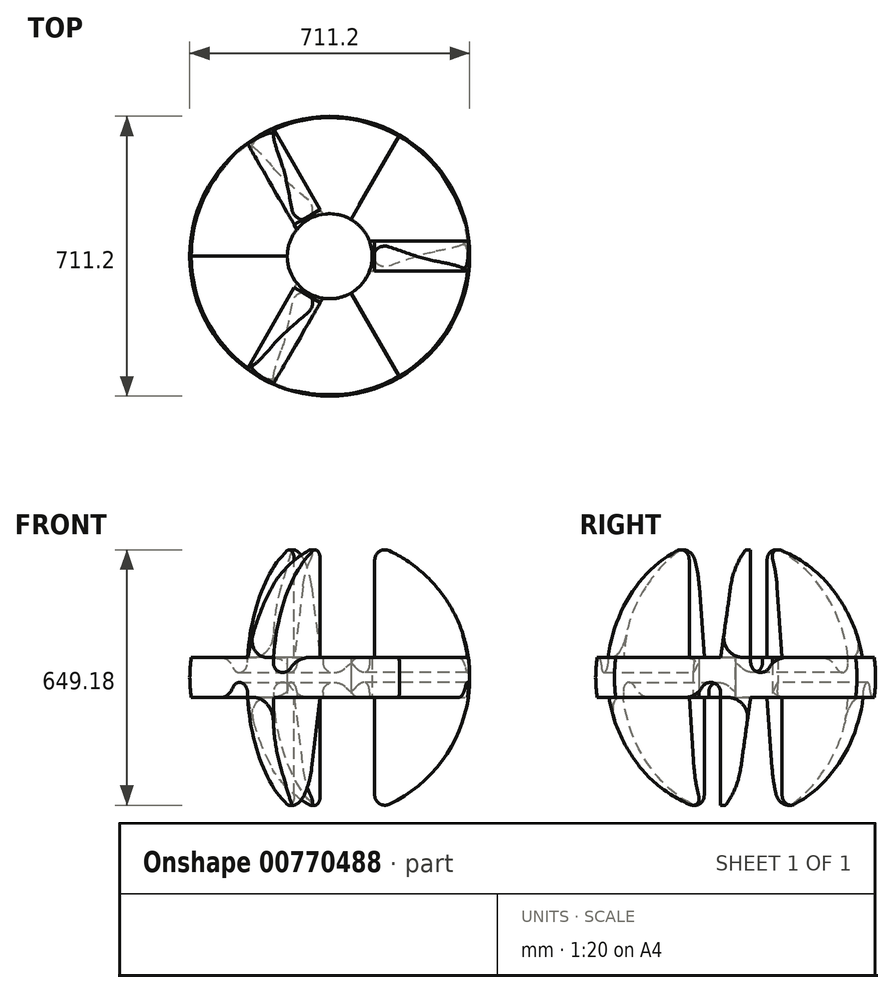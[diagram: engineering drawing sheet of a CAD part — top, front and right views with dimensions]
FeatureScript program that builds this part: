
annotation { "Feature Type Name" : "Feature", "Feature Type Description" : "" }
export const myFeature = defineFeature(function(context is Context, id is Id, definition is map)
    precondition{}
    {
        {
            var Q0;
            Q0=qCreatedBy(makeId("Front.planeOp"),FACE);
            var sketch = newSketch(context, id + "F0", { "sketchPlane" : qUnion([Q0])});
            skLineSegment(sketch, "E0", {"start": v(0, 0) * mm, "end": v(0, 719.83) * mm, "construction": true});
            skLineSegment(sketch, "E1", {"start": v(381, 750.81) * mm, "end": v(381, -112.59) * mm, "construction": true});
            skLineSegment(sketch, "E2", {"start": v(-124.84, 649.18) * mm, "end": v(765.44, 649.18) * mm, "construction": true});
            skLineSegment(sketch, "E3", {"start": v(114.3, 25.4) * mm, "end": v(114.3, 273.8) * mm});
            skLineSegment(sketch, "E4", {"start": v(107.95, 375.4) * mm, "end": v(107.95, 273.8) * mm});
            skLineSegment(sketch, "E5", {"start": v(0, 324.6) * mm, "end": v(640.71, 324.6) * mm, "construction": true});
            skLineSegment(sketch, "E6", {"start": v(351.95, 273.8) * mm, "end": v(114.3, 273.8) * mm});
            skLineSegment(sketch, "E7", {"start": v(114.3, 375.4) * mm, "end": v(351.95, 375.4) * mm});
            skArc(sketch, "E8", {"start": v(351.95, 273.8) * mm, "mid": v(355.6, 324.6) * mm, "end": v(351.95, 375.4) * mm});
            skArc(sketch, "E9.trimOffspring", {"start": v(150.45, 2.39) * mm, "mid": v(285.51, 112.61) * mm, "end": v(351.95, 273.8) * mm});
            skLineSegment(sketch, "E10.trimOffspring", {"start": v(114.3, 375.4) * mm, "end": v(114.3, 623.78) * mm});
            skLineSegment(sketch, "E11", {"start": v(107.95, 273.8) * mm, "end": v(114.3, 273.8) * mm});
            skLineSegment(sketch, "E12", {"start": v(107.95, 375.4) * mm, "end": v(114.3, 375.4) * mm});
            skArc(sketch, "E13.filletArc", {"start": v(114.3, 25.4) * mm, "mid": v(126.06, 3.97) * mm, "end": v(150.45, 2.39) * mm});
            skArc(sketch, "E14.filletArc", {"start": v(150.45, 646.8) * mm, "mid": v(126.06, 645.2) * mm, "end": v(114.3, 623.78) * mm});
            skArc(sketch, "E15", {"start": v(351.95, 375.4) * mm, "mid": v(285.51, 536.57) * mm, "end": v(150.45, 646.8) * mm});
            skSolve(sketch);
        }
        {
            var Q0;
            Q0=makeQuery(id+"F0.imprint","IMPRINT",FACE,{"disambiguationData":[TD([[makeQuery(id+"F0.imprint","IMPRINT",EDGE,{"derivedFrom":sQuery(id+"F0.wireOp",EDGE,"E4")}),1.0]])]});
            var Q1;
            Q1=sQuery(id+"F0.wireOp",EDGE,"E0");
            revolve(context, id + "F1", {"surfaceOperationType" : NewSurfaceOperationType.NEW, "entities" : qUnion([Q0]), "axis" : qUnion([Q1]), "revolveType" : RevolveType.SYMMETRIC, "angle" : 120 * degree});
        }
        {
            var Q0;
            Q0=makeQuery(id+"F0.imprint","IMPRINT",FACE,{"disambiguationData":[TD([[makeQuery(id+"F0.imprint","IMPRINT",EDGE,{"derivedFrom":sQuery(id+"F0.wireOp",EDGE,"E7")}),1.0]])]});
            var Q1;
            Q1=makeQuery(id+"F0.imprint","IMPRINT",FACE,{"disambiguationData":[TD([[makeQuery(id+"F0.imprint","IMPRINT",EDGE,{"derivedFrom":sQuery(id+"F0.wireOp",EDGE,"E3")}),-1.0]])]});
            extrude(context, id + "F2", {"entities" : qUnion([Q0, Q1]), "operationType" : NewBodyOperationType.ADD, "endBound" : BoundingType.SYMMETRIC, "depth" : 76.2 * mm, "offsetDistance" : 25.4 * mm});
        }
        {
            var Q0;
            Q0=qCreatedBy(makeId("Right.planeOp"),FACE);
            var sketch = newSketch(context, id + "F3", { "sketchPlane" : qUnion([Q0])});
            skLineSegment(sketch, "E16", {"start": v(-12.7, 556.07) * mm, "end": v(-38.1, 375.4) * mm});
            skCircle(sketch, "E17", {"center": v(0, 324.6) * mm, "radius": 355.6 * mm, "construction": true});
            skLineSegment(sketch, "E18", {"start": v(0, 324.6) * mm, "end": v(-249.76, 757.18) * mm, "construction": true});
            skLineSegment(sketch, "E19", {"start": v(-114.3, 705.13) * mm, "end": v(-114.3, 114.82) * mm, "construction": true});
            skLineSegment(sketch, "E20", {"start": v(-38.1, 375.4) * mm, "end": v(-89.45, 375.4) * mm});
            skLineSegment(sketch, "E21", {"start": v(-89.45, 375.4) * mm, "end": v(-89.45, 729.88) * mm});
            skLineSegment(sketch, "E22", {"start": v(121.26, 273.8) * mm, "end": v(38.1, 273.8) * mm});
            skLineSegment(sketch, "E23", {"start": v(38.1, 273.8) * mm, "end": v(12.7, 93.11) * mm});
            skLineSegment(sketch, "E24", {"start": v(121.26, -81.8) * mm, "end": v(121.26, 273.8) * mm});
            skArc(sketch, "E25", {"start": v(-12.7, 556.07) * mm, "mid": v(47.38, 673.98) * mm, "end": v(167.32, 729.88) * mm});
            skLineSegment(sketch, "E26", {"start": v(167.32, 729.88) * mm, "end": v(-89.45, 729.88) * mm});
            skArc(sketch, "E27", {"start": v(12.7, 93.11) * mm, "mid": v(-55.2, -31.96) * mm, "end": v(-188.52, -81.8) * mm});
            skLineSegment(sketch, "E28", {"start": v(-188.52, -81.8) * mm, "end": v(121.26, -81.8) * mm});
            skCircle(sketch, "E29", {"center": v(63.5, 362.7) * mm, "radius": 25.4 * mm});
            skCircle(sketch, "E30", {"center": v(-63.5, 286.5) * mm, "radius": 25.4 * mm});
            skLineSegment(sketch, "E31.bottom", {"start": v(88.9, 362.7) * mm, "end": v(38.1, 362.7) * mm});
            skLineSegment(sketch, "E31.top", {"start": v(88.9, 413.5) * mm, "end": v(38.1, 413.5) * mm});
            skLineSegment(sketch, "E31.left", {"start": v(88.9, 362.7) * mm, "end": v(88.9, 413.5) * mm});
            skLineSegment(sketch, "E31.right", {"start": v(38.1, 362.7) * mm, "end": v(38.1, 413.5) * mm});
            skLineSegment(sketch, "E32.bottom", {"start": v(-38.1, 286.5) * mm, "end": v(-88.9, 286.5) * mm});
            skLineSegment(sketch, "E32.top", {"start": v(-38.1, 235.7) * mm, "end": v(-88.9, 235.7) * mm});
            skLineSegment(sketch, "E32.left", {"start": v(-38.1, 286.5) * mm, "end": v(-38.1, 235.7) * mm});
            skLineSegment(sketch, "E32.right", {"start": v(-88.9, 286.5) * mm, "end": v(-88.9, 235.7) * mm});
            skSolve(sketch);
        }
        {
            var Q0;
            Q0=makeQuery(id+"F3.imprint","IMPRINT",FACE,{"disambiguationData":[TD([[makeQuery(id+"F3.imprint","IMPRINT",EDGE,{"derivedFrom":sQuery(id+"F3.wireOp",EDGE,"E16")}),-1.0]])]});
            var Q1;
            Q1=makeQuery(id+"F3.imprint","IMPRINT",FACE,{"disambiguationData":[TD([[makeQuery(id+"F3.imprint","IMPRINT",EDGE,{"derivedFrom":sQuery(id+"F3.wireOp",EDGE,"E22")}),1.0]])]});
            extrude(context, id + "F4", {"entities" : qUnion([Q0, Q1]), "operationType" : NewBodyOperationType.REMOVE, "endBound" : BoundingType.THROUGH_ALL, "depth" : 25.4 * mm, "offsetDistance" : 25.4 * mm});
        }
        {
            var Q0;
            Q0=makeQuery(id+"F3.imprint","IMPRINT",FACE,{"disambiguationData":[TD([[makeQuery(id+"F3.imprint","IMPRINT",EDGE,{"derivedFrom":sQuery(id+"F3.wireOp",EDGE,"E29")}),1.0]])]});
            var Q1;
            Q1=makeQuery(id+"F3.imprint","IMPRINT",FACE,{"disambiguationData":[TD([[makeQuery(id+"F3.imprint","IMPRINT",EDGE,{"derivedFrom":sQuery(id+"F3.wireOp",EDGE,"E30")}),1.0]])]});
            var Q2;
            Q2=makeQuery(id+"F3.imprint","IMPRINT",FACE,{"disambiguationData":[TD([[makeQuery(id+"F3.imprint","IMPRINT",EDGE,{"derivedFrom":sQuery(id+"F3.wireOp",EDGE,"E32.top")}),-1.0]])]});
            var Q3;
            Q3=makeQuery(id+"F3.imprint","IMPRINT",FACE,{"disambiguationData":[TD([[makeQuery(id+"F3.imprint","IMPRINT",EDGE,{"derivedFrom":sQuery(id+"F3.wireOp",EDGE,"E31.top")}),1.0]])]});
            extrude(context, id + "F5", {"entities" : qUnion([Q0, Q1, Q2, Q3]), "operationType" : NewBodyOperationType.REMOVE, "depth" : 355.6 * mm, "offsetDistance" : 25.4 * mm});
        }
        {
            var Q0;
            {var subQ0=sQuery(id+"F0.wireOp",EDGE,"E7");Q0=makeQuery(id+"F4.boolean.opBoolean","MERGE",EDGE,{"derivedFrom":[makeQuery(id+"F2.boolean.opBoolean","SPLIT",EDGE,{"disambiguationData":[topologyDisambiguationEdgeConnected([makeQuery(id+"F1.opRevolve","SWEPT_FACE",FACE,{"disambiguationData":[OSD([subQ0,sQuery(id+"F0.wireOp",EDGE,"E12")])]})])],"derivedFrom":makeQuery(id+"F2.opExtrude","CAP_EDGE",EDGE,{"disambiguationData":[OSD([subQ0])],"isStart":false})}),makeQuery(id+"F4.opExtrude","SWEPT_EDGE",EDGE,{"disambiguationData":[OSD([sQuery(id+"F3.wireOp",EDGE,"E16"),sQuery(id+"F3.wireOp",EDGE,"E20")])]})]});}
            var Q1;
            Q1=makeQuery(id+"F5.boolean.opBoolean","INTERSECT",EDGE,{"derivedFrom":[makeQuery(id+"F1.opRevolve","SWEPT_FACE",FACE,{"disambiguationData":[OSD([sQuery(id+"F0.wireOp",EDGE,"E7"),sQuery(id+"F0.wireOp",EDGE,"E12")])]}),makeQuery(id+"F5.opExtrude","SWEPT_FACE",FACE,{"disambiguationData":[OSD([sQuery(id+"F3.wireOp",EDGE,"E31.left")])]})]});
            var Q2;
            Q2=makeQuery(id+"F5.boolean.opBoolean","INTERSECT",EDGE,{"derivedFrom":[makeQuery(id+"F1.opRevolve","SWEPT_FACE",FACE,{"disambiguationData":[OSD([sQuery(id+"F0.wireOp",EDGE,"E6"),sQuery(id+"F0.wireOp",EDGE,"E11")])]}),makeQuery(id+"F5.opExtrude","SWEPT_FACE",FACE,{"disambiguationData":[OSD([sQuery(id+"F3.wireOp",EDGE,"E32.right")])]})]});
            var Q3;
            {var subQ0=sQuery(id+"F0.wireOp",EDGE,"E6");Q3=makeQuery(id+"F4.boolean.opBoolean","MERGE",EDGE,{"derivedFrom":[makeQuery(id+"F2.boolean.opBoolean","SPLIT",EDGE,{"disambiguationData":[topologyDisambiguationEdgeConnected([makeQuery(id+"F1.opRevolve","SWEPT_FACE",FACE,{"disambiguationData":[OSD([subQ0,sQuery(id+"F0.wireOp",EDGE,"E11")])]})])],"derivedFrom":makeQuery(id+"F2.opExtrude","CAP_EDGE",EDGE,{"disambiguationData":[OSD([subQ0])],"isStart":true})}),makeQuery(id+"F4.opExtrude","SWEPT_EDGE",EDGE,{"disambiguationData":[OSD([sQuery(id+"F3.wireOp",EDGE,"E22"),sQuery(id+"F3.wireOp",EDGE,"E23")])]})]});}
            fillet(context, id + "F6", {"entities" : qUnion([Q0, Q1, Q2, Q3]), "radius" : 50.8 * mm, "tangentPropagation" : true, "allowEdgeOverflow" : false});
        }
        {
            var Q0;
            Q0=makeQuery(id+"F1.opRevolve","SWEPT_BODY",BODY,{"disambiguationData":[OSD([sQuery(id+"F0.wireOp",EDGE,"E4"),sQuery(id+"F0.wireOp",EDGE,"E6"),sQuery(id+"F0.wireOp",EDGE,"E7"),sQuery(id+"F0.wireOp",EDGE,"E8"),sQuery(id+"F0.wireOp",EDGE,"E11"),sQuery(id+"F0.wireOp",EDGE,"E12")])]});
            var Q1;
            Q1=sQuery(id+"F0.wireOp",EDGE,"E0");
            circularPattern(context, id + "F7", {"entities" : qUnion([Q0]), "axis" : qUnion([Q1]), "angle" : 360 * degree, "instanceCount" : 3, "equalSpace" : true});
        }
    });
